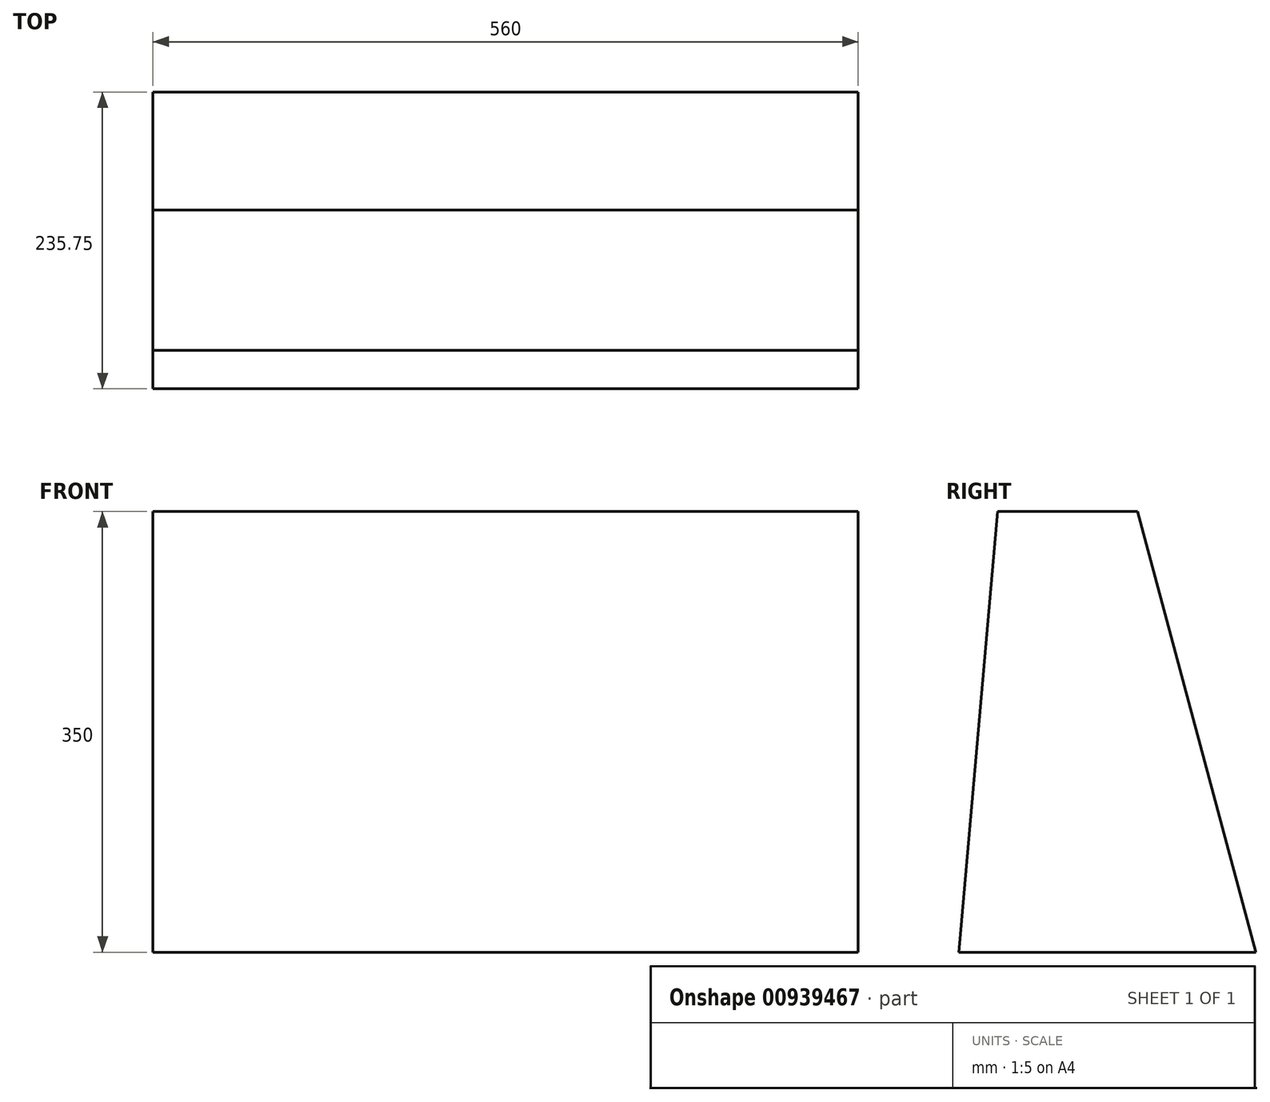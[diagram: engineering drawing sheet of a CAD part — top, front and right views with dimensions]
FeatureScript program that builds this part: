
annotation { "Feature Type Name" : "Feature", "Feature Type Description" : "" }
export const myFeature = defineFeature(function(context is Context, id is Id, definition is map)
    precondition{}
    {
        {
            var Q0;
            Q0=qCreatedBy(makeId("Right.planeOp"),FACE);
            var sketch = newSketch(context, id + "F0", { "sketchPlane" : qUnion([Q0])});
            skLineSegment(sketch, "E0", {"start": v(0, 0) * mm, "end": v(30.62, 350) * mm});
            skLineSegment(sketch, "E1", {"start": v(30.62, 350) * mm, "end": v(141.96, 350) * mm});
            skLineSegment(sketch, "E2", {"start": v(141.96, 350) * mm, "end": v(277.28, -155) * mm});
            skLineSegment(sketch, "E3", {"start": v(277.28, -155) * mm, "end": v(172.28, -155) * mm});
            skLineSegment(sketch, "E4", {"start": v(100, 0) * mm, "end": v(0, 0) * mm});
            skLineSegment(sketch, "E5", {"start": v(100, 0) * mm, "end": v(172.28, -155) * mm});
            skSolve(sketch);
        }
        {
            var Q0;
            Q0 = qSketchRegion(id + "F0", true);
            extrude(context, id + "F1", {"entities" : qUnion([Q0]), "endBound" : BoundingType.SYMMETRIC, "depth" : 560 * mm, "offsetDistance" : 25 * mm});
        }
        {
            var Q0;
            Q0=makeQuery(id+"F1.opExtrude","CAP_FACE",FACE,{"disambiguationData":[OSD([sQuery(id+"F0.wireOp",EDGE,"E0"),sQuery(id+"F0.wireOp",EDGE,"E1"),sQuery(id+"F0.wireOp",EDGE,"E2"),sQuery(id+"F0.wireOp",EDGE,"E3"),sQuery(id+"F0.wireOp",EDGE,"E4"),sQuery(id+"F0.wireOp",EDGE,"E5")])],"isStart":true});
            var sketch = newSketch(context, id + "F2", { "sketchPlane" : qUnion([Q0])});
            skLineSegment(sketch, "E6.0", {"start": v(-100, 0) * mm, "end": v(-172.28, -155) * mm});
            skLineSegment(sketch, "E6.1", {"start": v(-277.28, -155) * mm, "end": v(-172.28, -155) * mm});
            skLineSegment(sketch, "E6.2", {"start": v(-235.75, 0) * mm, "end": v(-277.28, -155) * mm});
            skPoint(sketch, "E6.3", {"position": v(-224.78, -155) * mm});
            skLineSegment(sketch, "E7", {"start": v(-100, 0) * mm, "end": v(-235.75, 0) * mm});
            skPoint(sketch, "E8.orphan", {"position": v(-141.96, 350) * mm});
            skSolve(sketch);
        }
        {
            var Q0;
            Q0 = qSketchRegion(id + "F2", true);
            extrude(context, id + "F3", {"entities" : qUnion([Q0]), "operationType" : NewBodyOperationType.REMOVE, "endBound" : BoundingType.THROUGH_ALL, "oppositeDirection" : true, "depth" : 200 * mm, "offsetDistance" : 25 * mm});
        }
    });
